# Revit family: Double_Check_Valve_Assemblies-WATTS-(125-200_LF007-QT, 125-200_LF007-QT-S)_Series
name_source: partatom
category: Pipe Accessories
units: mm (PartAtom-declared; Revit-internal decimal feet)

## family parameters
Always vertical = Yes
Cut with Voids When Loaded = No
OmniClass Number = 23.65.55.14.21
OmniClass Title = Non-Return Valves for Liquid Services
Part Type = Valve - Breaks Into
Round Connector Dimension = Use Radius
Shared = No
Work Plane-Based = No

## types (6) — shared parameters
Assembly Code = D2090900
BV_Handle_Angle = 45.00°
Body_Ang1 = 45.00°
Compliance Certifications = ASSE, AWWA, IAPMO, CSA, UPC
Connection Type = Female NPT Connection
Connection_Rad = 1"
Country = United States
Cover_AF = 2 3/8"
Description = Lead Free* Double Check Valve Assembly Backflow Preventers with Freeze Sensor
FZ Freeze sensor = No
Finish = Metal-WATTS-Cast Copper Silicon Alloy
Flow Rate = 7.5 fps / 2.3 mps
LF Without shutoff valves = No
Manufacturer = WATTS
Manufacturer Product Line = Backflow Prevention
Material = Metal-WATTS-Cast Copper Silicon Alloy
Pressure Rating = 175.00 psi
Product Documentation Link = https://www.watts.com
Product Page URL = https://www.watts.com
Region = North America
Revised Date = 12/11/2023
STR_Angle = 45.00°
TC1_Dist = 7/8"
TC_Body_Height = 15/16"
TC_Body_Rad = 13/32"
TC_Boss_Rad = 3/8"
TC_In_Thd_Length = 9/32"
TC_In_Thd_Rad = 9/32"
TC_Out_Thd_Length = 13/32"
TC_Out_Thd_Rad = 11/32"
Temperature Range = 33˚F – 180°F (0.5˚C – 82°C)
U Union connections = No
URL = http://www.watts.com
W/Press** Press inlet x press outlet = No

## per-type parameters (varying)
- LF007-M2-QT-S - 1.25": A Dimension=16 3/8"; As Dimension=21 1/2"; B Dimension=5"; BV1_OAL=3 7/16"; BV1_Stem_Dist=1 15/16"; BV2_OAL=3 7/16"; BV2_Stem_Dist=1 21/32"; BV_Body_Rad=1 5/32"; BV_Handle_CL_Angle=19/32"; BV_Handle_CL_Front=21/32"; BV_Handle_Hieght=15/16"; BV_Handle_Length=5 1/16"; BV_Handle_Thk=1/8"; BV_Handle_Width_Btm=-15/32"; BV_Handle_Width_Top=15/32"; BV_Stem_Hieght=1 31/32"; BV_Stem_Rad=15/32"; Body_Ang2=25.00°; Body_IN_Ang1=1 1/32"; Body_IN_Ang2=7 3/16"; Body_Rad=1 17/32"; Body_Step_Rad=1 1/16"; Body_Thd_Rad=27/32"; Bs Dimension=7 1/16"; C Dimension=3 5/16"; Connection Size=1 1/4"; Cover_Dist=3 13/16"; Cover_Ext_Dist=-5/8"; Cover_Hieght=1 3/4"; Cover_Rad=5/16"; Cover_Thk=5/8"; D Dimension=3 1/2"; F Dimension=9 1/2"; G Dimension=5"; Height=3 5/16"; IN_Thd_Length=13/32"; Inlet Connection Description=1 1/4" Inlet Connection; Length=21 1/2"; OUT_Thd_Length=3/8"; Outlet Connection Description=1 1/4" Outlet Connection; Pipe Connection Distance=4 11/32"; R Dimension=3"; S Copper silicon alloy strainer=Yes; STR_Flow_Rad=31/32"; STR_IN_Port=1 13/32"; STR_Main_Rad=1 1/32"; STR_Nipple_OAL=25/32"; STR_Nipple_Rad=27/32"; STR_OAL=4 11/32"; STR_Port_Length=4"; STR_Screen_Length=3 3/4"; Shipping Weight=19.00 lb; T Dimension=2"; TC1_Boss_Height=1 7/16"; TC2_Boss_Height=1 17/32"; TC2_Dist=4 19/32"; TC3_Boss_Height=1 3/4"; TC3_Dist=7 1/4"; TC4_Boss_Height=1 17/32"; TC4_Dist=11 13/32"; Valve_OAL=9 1/2"
- LF007-M2-QT-S - 1.5": A Dimension=16 3/4"; As Dimension=21 3/4"; B Dimension=4 7/8"; BV1_OAL=3 1/2"; BV1_Stem_Dist=2 5/32"; BV2_OAL=3 1/2"; BV2_Stem_Dist=1 27/32"; BV_Body_Rad=1 1/4"; BV_Handle_CL_Angle=23/32"; BV_Handle_CL_Front=25/32"; BV_Handle_Hieght=31/32"; BV_Handle_Length=5 27/32"; BV_Handle_Thk=5/32"; BV_Handle_Width_Btm=-15/32"; BV_Handle_Width_Top=15/32"; BV_Stem_Hieght=2 9/32"; BV_Stem_Rad=19/32"; Body_Ang2=25.00°; Body_IN_Ang1=1 1/32"; Body_IN_Ang2=7 3/16"; Body_Rad=1 17/32"; Body_Step_Rad=1 1/16"; Body_Thd_Rad=15/16"; Bs Dimension=7 1/16"; C Dimension=3 5/16"; Connection Size=1 1/2"; Cover_Dist=3 13/16"; Cover_Ext_Dist=-5/8"; Cover_Hieght=1 3/4"; Cover_Rad=5/16"; Cover_Thk=5/8"; D Dimension=3 3/4"; F Dimension=9 3/4"; G Dimension=5 13/16"; Height=3 1/2"; IN_Thd_Length=7/16"; Inlet Connection Description=1 1/2" Inlet Connection; Length=25 1/16"; OUT_Thd_Length=7/16"; Outlet Connection Description=1 1/2" Outlet Connection; Pipe Connection Distance=5 27/32"; R Dimension=3 1/8"; S Copper silicon alloy strainer=Yes; STR_Flow_Rad=1 3/32"; STR_IN_Port=1 5/8"; STR_Main_Rad=1 7/32"; STR_Nipple_OAL=2 15/32"; STR_Nipple_Rad=15/16"; STR_OAL=5 27/32"; STR_Port_Length=4 3/32"; STR_Screen_Length=3"; Shipping Weight=19.60 lb; T Dimension=2 11/16"; TC1_Boss_Height=1 9/16"; TC2_Boss_Height=1 17/32"; TC2_Dist=4 1/2"; TC3_Boss_Height=1 3/4"; TC3_Dist=7 3/8"; TC4_Boss_Height=1 17/32"; TC4_Dist=11 3/4"; Valve_OAL=9 3/4"
- LF007-M1-QT-S - 2": A Dimension=19 1/2"; As Dimension=25 3/4"; B Dimension=6 1/4"; BV1_OAL=3 1/16"; BV1_Stem_Dist=2 13/32"; BV2_OAL=3 1/16"; BV2_Stem_Dist=2 1/8"; BV_Body_Rad=1 19/32"; BV_Handle_CL_Angle=23/32"; BV_Handle_CL_Front=25/32"; BV_Handle_Hieght=31/32"; BV_Handle_Length=6 7/16"; BV_Handle_Thk=5/32"; BV_Handle_Width_Btm=-17/32"; BV_Handle_Width_Top=17/32"; BV_Stem_Hieght=2 19/32"; BV_Stem_Rad=19/32"; Body_Ang2=30.00°; Body_IN_Ang1=1 5/16"; Body_IN_Ang2=8 11/32"; Body_Rad=1 7/8"; Body_Step_Rad=1 1/4"; Body_Thd_Rad=1 3/16"; Bs Dimension=8 3/4"; C Dimension=4"; Connection Size=2"; Cover_Dist=4 9/16"; Cover_Ext_Dist=-19/32"; Cover_Hieght=2 11/32"; Cover_Rad=2 3/8"; Cover_Thk=19/32"; D Dimension=4"; F Dimension=13 3/8"; G Dimension=6 1/8"; Height=4"; IN_Thd_Length=15/32"; Inlet Connection Description=2" Inlet Connection; Length=27 1/4"; OUT_Thd_Length=15/32"; Outlet Connection Description=2" Outlet Connection; Pipe Connection Distance=6 3/16"; R Dimension=3 7/16"; S Copper silicon alloy strainer=Yes; STR_Flow_Rad=1 3/8"; STR_IN_Port=1 1/2"; STR_Main_Rad=1 17/32"; STR_Nipple_OAL=1 9/16"; STR_Nipple_Rad=1 3/16"; STR_OAL=6 3/16"; STR_Port_Length=4 3/32"; STR_Screen_Length=4 5/32"; Shipping Weight=33.50 lb; T Dimension=2 11/16"; TC1_Boss_Height=1 13/16"; TC2_Boss_Height=2 3/16"; TC2_Dist=4 3/4"; TC3_Boss_Height=2 11/32"; TC3_Dist=7 5/8"; TC4_Boss_Height=2 3/16"; TC4_Dist=12 1/2"; Valve_OAL=13 3/8"
- LF007-M1-QT- 2": A Dimension=19 1/2"; As Dimension=25 3/4"; B Dimension=6 1/4"; BV1_OAL=3 1/16"; BV1_Stem_Dist=2 13/32"; BV2_OAL=3 1/16"; BV2_Stem_Dist=2 1/8"; BV_Body_Rad=1 19/32"; BV_Handle_CL_Angle=23/32"; BV_Handle_CL_Front=25/32"; BV_Handle_Hieght=31/32"; BV_Handle_Length=6 7/16"; BV_Handle_Thk=5/32"; BV_Handle_Width_Btm=-17/32"; BV_Handle_Width_Top=17/32"; BV_Stem_Hieght=2 19/32"; BV_Stem_Rad=19/32"; Body_Ang2=30.00°; Body_IN_Ang1=1 5/16"; Body_IN_Ang2=8 11/32"; Body_Rad=1 7/8"; Body_Step_Rad=1 1/4"; Body_Thd_Rad=1 3/16"; Bs Dimension=8 3/4"; C Dimension=4"; Connection Size=2"; Cover_Dist=4 9/16"; Cover_Ext_Dist=-19/32"; Cover_Hieght=2 11/32"; Cover_Rad=2 3/8"; Cover_Thk=19/32"; D Dimension=4"; F Dimension=13 3/8"; G Dimension=6 1/8"; Height=4"; IN_Thd_Length=15/32"; Inlet Connection Description=2" Inlet Connection; Length=27 1/4"; OUT_Thd_Length=15/32"; Outlet Connection Description=2" Outlet Connection; Pipe Connection Distance=0"; R Dimension=3 7/16"; S Copper silicon alloy strainer=No; STR_Flow_Rad=1 3/8"; STR_IN_Port=1 1/2"; STR_Main_Rad=1 17/32"; STR_Nipple_OAL=1 9/16"; STR_Nipple_Rad=1 3/16"; STR_OAL=6 3/16"; STR_Port_Length=4 3/32"; STR_Screen_Length=4 5/32"; Shipping Weight=25.70 lb; T Dimension=2 11/16"; TC1_Boss_Height=1 13/16"; TC2_Boss_Height=2 3/16"; TC2_Dist=4 3/4"; TC3_Boss_Height=2 11/32"; TC3_Dist=7 5/8"; TC4_Boss_Height=2 3/16"; TC4_Dist=12 1/2"; Valve_OAL=13 3/8"
- LF007-M2-QT- 1.25": A Dimension=16 3/8"; As Dimension=21 1/2"; B Dimension=5"; BV1_OAL=3 7/16"; BV1_Stem_Dist=1 15/16"; BV2_OAL=3 7/16"; BV2_Stem_Dist=1 21/32"; BV_Body_Rad=1 5/32"; BV_Handle_CL_Angle=19/32"; BV_Handle_CL_Front=21/32"; BV_Handle_Hieght=15/16"; BV_Handle_Length=5 1/16"; BV_Handle_Thk=1/8"; BV_Handle_Width_Btm=-15/32"; BV_Handle_Width_Top=15/32"; BV_Stem_Hieght=1 31/32"; BV_Stem_Rad=15/32"; Body_Ang2=25.00°; Body_IN_Ang1=1 1/32"; Body_IN_Ang2=7 3/16"; Body_Rad=1 17/32"; Body_Step_Rad=1 1/16"; Body_Thd_Rad=27/32"; Bs Dimension=7 1/16"; C Dimension=3 5/16"; Connection Size=1 1/4"; Cover_Dist=3 13/16"; Cover_Ext_Dist=-5/8"; Cover_Hieght=1 3/4"; Cover_Rad=5/16"; Cover_Thk=5/8"; D Dimension=3 1/2"; F Dimension=9 1/2"; G Dimension=5"; Height=3 5/16"; IN_Thd_Length=13/32"; Inlet Connection Description=1 1/4" Inlet Connection; Length=21 1/2"; OUT_Thd_Length=3/8"; Outlet Connection Description=1 1/4" Outlet Connection; Pipe Connection Distance=0"; R Dimension=3"; S Copper silicon alloy strainer=No; STR_Flow_Rad=31/32"; STR_IN_Port=1 13/32"; STR_Main_Rad=1 1/32"; STR_Nipple_OAL=25/32"; STR_Nipple_Rad=27/32"; STR_OAL=4 11/32"; STR_Port_Length=4"; STR_Screen_Length=3 3/4"; Shipping Weight=15.00 lb; T Dimension=2"; TC1_Boss_Height=1 7/16"; TC2_Boss_Height=1 17/32"; TC2_Dist=4 19/32"; TC3_Boss_Height=1 3/4"; TC3_Dist=7 1/4"; TC4_Boss_Height=1 17/32"; TC4_Dist=11 13/32"; Valve_OAL=9 1/2"
- LF007-M2-QT- 1.5": A Dimension=16 3/4"; As Dimension=21 3/4"; B Dimension=4 7/8"; BV1_OAL=3 1/2"; BV1_Stem_Dist=2 5/32"; BV2_OAL=3 1/2"; BV2_Stem_Dist=1 27/32"; BV_Body_Rad=1 1/4"; BV_Handle_CL_Angle=23/32"; BV_Handle_CL_Front=25/32"; BV_Handle_Hieght=31/32"; BV_Handle_Length=5 27/32"; BV_Handle_Thk=5/32"; BV_Handle_Width_Btm=-15/32"; BV_Handle_Width_Top=15/32"; BV_Stem_Hieght=2 9/32"; BV_Stem_Rad=19/32"; Body_Ang2=25.00°; Body_IN_Ang1=1 1/32"; Body_IN_Ang2=7 3/16"; Body_Rad=1 17/32"; Body_Step_Rad=1 1/16"; Body_Thd_Rad=15/16"; Bs Dimension=7 1/16"; C Dimension=3 5/16"; Connection Size=1 1/2"; Cover_Dist=3 13/16"; Cover_Ext_Dist=-5/8"; Cover_Hieght=1 3/4"; Cover_Rad=5/16"; Cover_Thk=5/8"; D Dimension=3 3/4"; F Dimension=9 3/4"; G Dimension=5 13/16"; Height=3 1/2"; IN_Thd_Length=7/16"; Inlet Connection Description=1 1/2" Inlet Connection; Length=25 1/16"; OUT_Thd_Length=7/16"; Outlet Connection Description=1 1/2" Outlet Connection; Pipe Connection Distance=0"; R Dimension=3 1/8"; S Copper silicon alloy strainer=No; STR_Flow_Rad=1 3/32"; STR_IN_Port=1 5/8"; STR_Main_Rad=1 7/32"; STR_Nipple_OAL=2 15/32"; STR_Nipple_Rad=15/16"; STR_OAL=5 27/32"; STR_Port_Length=4 3/32"; STR_Screen_Length=3"; Shipping Weight=15.90 lb; T Dimension=2 11/16"; TC1_Boss_Height=1 9/16"; TC2_Boss_Height=1 17/32"; TC2_Dist=4 1/2"; TC3_Boss_Height=1 3/4"; TC3_Dist=7 3/8"; TC4_Boss_Height=1 17/32"; TC4_Dist=11 3/4"; Valve_OAL=9 3/4"

note: column(s) folded — value = type name in every type: Model

## geometry (parser evidence)
native form markers: Sweep x6
no freeform markers — native parametric forms only
